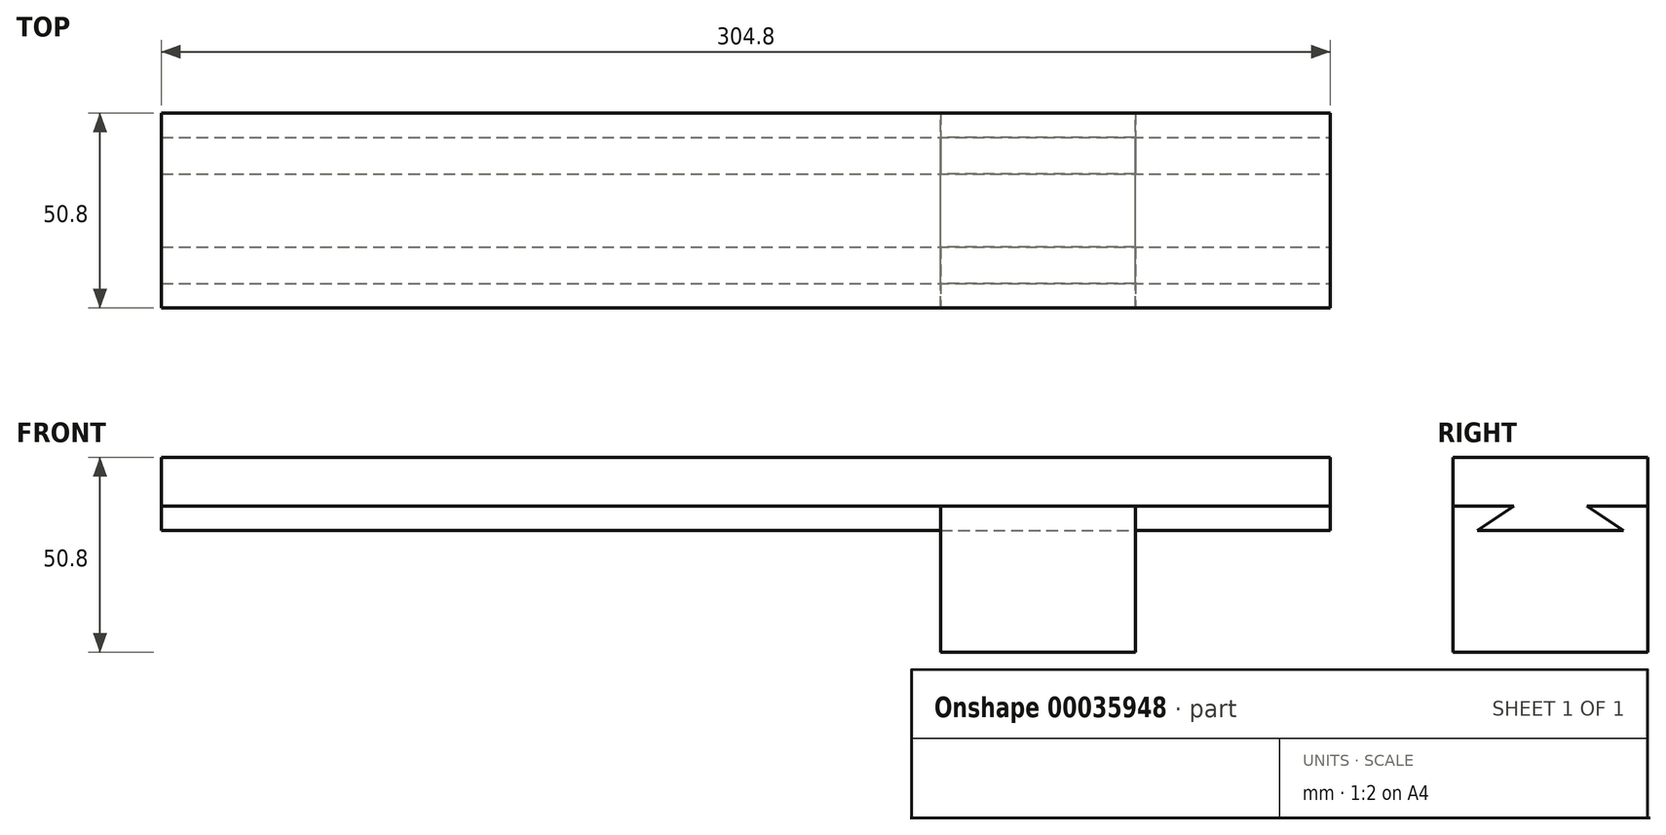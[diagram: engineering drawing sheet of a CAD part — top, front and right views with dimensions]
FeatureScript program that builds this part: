
annotation { "Feature Type Name" : "Feature", "Feature Type Description" : "" }
export const myFeature = defineFeature(function(context is Context, id is Id, definition is map)
    precondition{}
    {
        {
            var Q0;
            Q0=qCreatedBy(makeId("Top.planeOp"),FACE);
            var sketch = newSketch(context, id + "F0", { "sketchPlane" : qUnion([Q0])});
            skLineSegment(sketch, "E0.rect.bottom", {"start": v(152.4, 25.4) * mm, "end": v(-152.4, 25.4) * mm});
            skLineSegment(sketch, "E0.rect.top", {"start": v(152.4, -25.4) * mm, "end": v(-152.4, -25.4) * mm});
            skLineSegment(sketch, "E0.rect.left", {"start": v(152.4, 25.4) * mm, "end": v(152.4, -25.4) * mm});
            skLineSegment(sketch, "E0.rect.right", {"start": v(-152.4, 25.4) * mm, "end": v(-152.4, -25.4) * mm});
            skPoint(sketch, "E0.rect.middle", {"position": v(0, 0) * mm});
            skSolve(sketch);
        }
        {
            var Q0;
            Q0=makeQuery(id+"F0.imprint","IMPRINT",FACE,{"disambiguationData":[TD([[makeQuery(id+"F0.imprint","IMPRINT",EDGE,{"derivedFrom":sQuery(id+"F0.wireOp",EDGE,"E0.rect.bottom")}),1.0]])]});
            extrude(context, id + "F1", {"entities" : qUnion([Q0]), "endBound" : BoundingType.SYMMETRIC, "depth" : 12.7 * mm});
        }
        {
            var Q0;
            Q0=makeQuery(id+"F1.opExtrude","SWEPT_FACE",FACE,{"disambiguationData":[OSD([sQuery(id+"F0.wireOp",EDGE,"E0.rect.left")])]});
            var sketch = newSketch(context, id + "F2", { "sketchPlane" : qUnion([Q0])});
            skLineSegment(sketch, "E1", {"start": v(-9.53, -6.35) * mm, "end": v(-19.05, -12.7) * mm});
            skLineSegment(sketch, "E2", {"start": v(-19.05, -12.7) * mm, "end": v(19.05, -12.7) * mm});
            skLineSegment(sketch, "E3", {"start": v(19.05, -12.7) * mm, "end": v(9.52, -6.35) * mm});
            skLineSegment(sketch, "E4", {"start": v(9.52, -6.35) * mm, "end": v(-9.52, -6.35) * mm});
            skPoint(sketch, "E5", {"position": v(0, -12.7) * mm});
            skSolve(sketch);
        }
        {
            var Q0;
            Q0=makeQuery(id+"F2.imprint","IMPRINT",FACE,{"disambiguationData":[TD([[makeQuery(id+"F2.imprint","IMPRINT",EDGE,{"derivedFrom":sQuery(id+"F2.wireOp",EDGE,"E1")}),1.0]])]});
            var Q1;
            Q1=makeQuery(id+"F1.opExtrude","SWEPT_FACE",FACE,{"disambiguationData":[OSD([sQuery(id+"F0.wireOp",EDGE,"E0.rect.right")])]});
            extrude(context, id + "F3", {"entities" : qUnion([Q0]), "operationType" : NewBodyOperationType.ADD, "endBound" : BoundingType.UP_TO_SURFACE, "oppositeDirection" : true, "endBoundEntityFace" : qUnion([Q1]), "depth" : 25.4 * mm});
        }
        {
            var Q0;
            Q0=qCreatedBy(makeId("Right.planeOp"),FACE);
            cPlane(context, id + "F4", {"entities" : qUnion([Q0]), "cplaneType" : CPlaneType.OFFSET, "offset" : 76.2 * mm, "width" : 152.4 * mm, "height" : 152.4 * mm});
        }
        {
            var Q0;
            Q0=qCreatedBy(id+"F4.planeOp",FACE);
            var sketch = newSketch(context, id + "F5", { "sketchPlane" : qUnion([Q0])});
            skLineSegment(sketch, "E6.0", {"start": v(-9.52, -6.35) * mm, "end": v(-19.05, -12.7) * mm});
            skLineSegment(sketch, "E6.1", {"start": v(19.05, -12.7) * mm, "end": v(9.53, -6.35) * mm});
            skLineSegment(sketch, "E6.2", {"start": v(-19.05, -12.7) * mm, "end": v(19.05, -12.7) * mm});
            skLineSegment(sketch, "E6.3", {"start": v(-9.52, -6.35) * mm, "end": v(-25.4, -6.35) * mm});
            skLineSegment(sketch, "E6.4", {"start": v(25.4, -6.35) * mm, "end": v(9.53, -6.35) * mm});
            skLineSegment(sketch, "E7", {"start": v(-25.4, -6.35) * mm, "end": v(-25.4, -44.45) * mm});
            skLineSegment(sketch, "E8", {"start": v(-25.4, -44.45) * mm, "end": v(25.4, -44.45) * mm});
            skLineSegment(sketch, "E9", {"start": v(25.4, -44.45) * mm, "end": v(25.4, -6.35) * mm});
            skSolve(sketch);
        }
        {
            var Q0;
            Q0=makeQuery(id+"F5.imprint","IMPRINT",FACE,{"disambiguationData":[TD([[makeQuery(id+"F5.imprint","IMPRINT",EDGE,{"derivedFrom":sQuery(id+"F5.wireOp",EDGE,"E6.0")}),-1.0]])]});
            extrude(context, id + "F6", {"entities" : qUnion([Q0]), "endBound" : BoundingType.SYMMETRIC, "depth" : 50.8 * mm});
        }
    });
